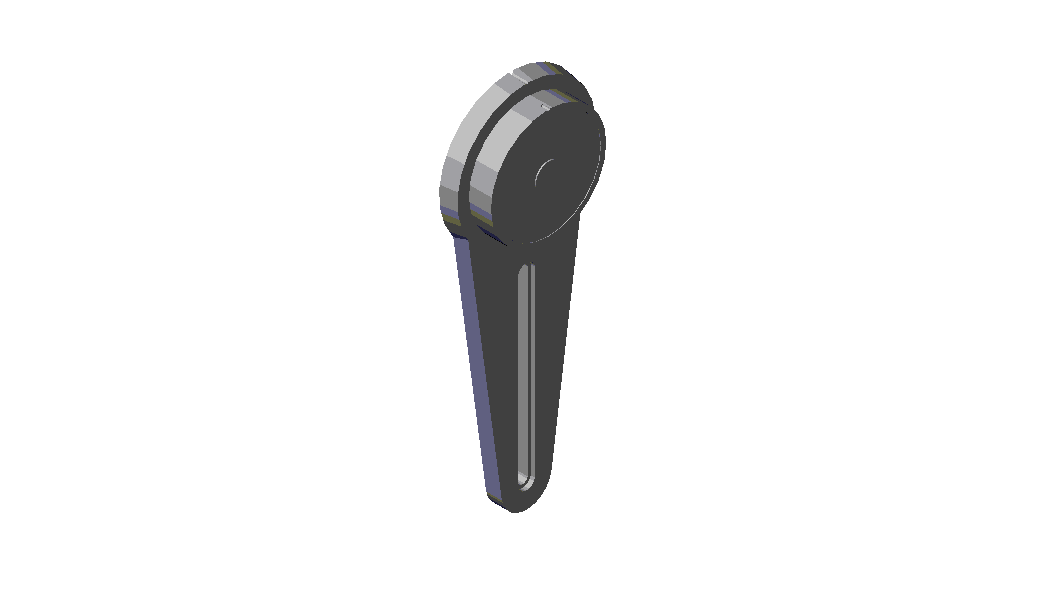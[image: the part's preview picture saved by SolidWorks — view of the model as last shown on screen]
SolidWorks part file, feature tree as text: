
SOLIDWORKS PART (.sldprt)
format: sldprt  version: not decoded by parser v0  size: 270,848 bytes
history: native  units: mm
features: sketch x6, cut_extrude x4, plane x3, material x1, revolve x1, extrude x1 (+8 scaffold rows collapsed)
feature tree (24):
  scaffold x8  (default folders/planes/origin — collapsed)
  material  "Matériau <non spécifié>"
  plane  "Face"
  plane  "Dessus"
  plane  "Droite"
  sketch  "Esquisse1"  dims[D1=68.5mm D2=66.0mm D3=55.0mm D4=50.0mm D5=12.5mm D6=7.5mm D7=10.25mm D8=10.5mm D9=0.5mm]
  revolve  "Révolution1"  Angle=360deg
  sketch  "Esquisse2"  dims[D2=1.5mm D1=27.5mm]
  cut_extrude  "Enlèv. mat.-Extru.1"  Depth=3.5mm
  sketch  "Esquisse3"  dims[D1=2.0mm D2=33.55mm]
  cut_extrude  "Enlèv. mat.-Extru.2"  [1 undecoded]
  sketch  "Esquisse4"  dims[D1=12.0mm D3=60.0mm D2=131.0mm D4=45.0mm D5=2.5mm]
  extrude  "Extrusion1"  Depth=7.5mm
  sketch  "Esquisse5"  dims[c1.D1=12.0mm c1.D2=12.0mm c1.D3=2.0mm c1.D4=~3.504539mm c1.D5=~74.958205mm c2.D4=2.0mm c2.D5=333.0mm c3.D5=90.0deg c4.D5=23.0mm c4.D6=4.5mm c4.D7=2.0mm c4.D8=2.0mm c4.D9=20.0mm c4.D10=21.0mm c4.D11=~153.57932mm c5.D11=~179.774419deg c6.D11=2.0mm c6.D12=22.5mm c6.D13=3.0mm]
  cut_extrude  "Enlèv. mat.-Extru.3"  Depth=3.5mm
  sketch  "Esquisse6"  dims[D1=8.0mm D2=8.0mm]
  cut_extrude  "Enlèv. mat.-Extru.4"  Depth=2mm
decode coverage: 11 of 12 modeling features carry decoded parameters
note: ~ marks probable driven/reference dimensions
note: 1 parameter value undecoded
note: suppression state not decoded; provenance and decode notes live in map.json
